# Revit family: QUEST_506_Dehumidifiers
name_source: partatom
category: Mechanical Equipment
revit_build: Autodesk Revit 2016 (Build: 20150714_1515(x64)
units: mm (PartAtom-declared; Revit-internal decimal feet)

## family parameters
Always vertical = Yes
Cut with Voids When Loaded = No
OmniClass Number = 23.75.00.00
OmniClass Title = Climate Control (HVAC)
Part Type = Normal
Room Calculation Point = No
Round Connector Dimension = Use Diameter
Shared = No
Work Plane-Based = No

## types (1)
- QUEST_506_Dehumidifiers
    Air Filter (MERV-13) (2) = Size: 18" x 20" x 2"
    Clearance = Yes
    Collar Plate = Yes
    Current Draw = 11.0
    Drain Connection = 3/4” Threaded Female NPT
    Efficiency = 8.1 Pints/kWh
    Energy Factor = 3.8 L/kWh
    Operating Temperature = 56°F Min - 95°F Max
    Power = 2700
    Power Cord = 14ga 10’, NEMA 6-20P
    Refrigerant = R410A
    Shipping Dimensions = 36”W x 40”H x 48”D
    Shipping Options = UPS and LTL
    Shipping Weight = 340 lbs.
    Supply Voltage = 220-240 VAC - 1 Phase - 60 Hz
    Trap = Yes
    URL = www.questclimate.com/product/quest-506/
    Unit Dimensions = 28.9”W x 33.8”H x 44.7”D
    Unit Weight = 280 lbs.
    Water Removal = 506 (Pints/Day)

## geometry (parser evidence)
native form markers: Sweep x2
no freeform markers — native parametric forms only
